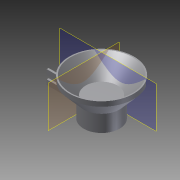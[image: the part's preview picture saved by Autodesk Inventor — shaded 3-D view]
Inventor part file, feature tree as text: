
AUTODESK INVENTOR PART (.ipt)
format: ipt  version: 2012 (Build 160160000, 160)  size: 119,808 bytes
history: native  units: in
note: dims shown in document units (in); Inventor stores cm internally (conversion verified against a paired STEP export)
features: plane x3, sketch x3, reference x3, extrude x2, revolve x1
ambient origin geometry x8: Origin, YZ Plane, XZ Plane, XY Plane, X Axis, Y Axis, Z Axis, Center Point
bodies: Solid1 (feature_tree)
feature tree (12):
  revolve  "Revolution1"  [1 undecoded]
  plane  "Work Plane1"
  extrude  "Extrusion1"  Depth=0.0394in
  plane  "Work Plane3"
  extrude  "Extrusion2"  Depth=0.0812in TaperAngle=0.0deg
  sketch  "Sketch1"  dims[d0=90.0deg d1=0.1969in]
  reference  "Reference1"
  sketch  "Sketch2"  dims[d2=0.0787in d3=0.0394in]
  reference  "Reference2"
  plane  "Work Plane2"
  sketch  "Sketch3"  dims[d4=0.1575in d6=0.0812in d7=1.5094in d8=0.0in d9=0.0in d10=0.0197in d11=0.4562in d12=0.2281in d13=0.0in d14=0.0in]
  reference  "Reference3"
note: 1 required parameter value undecoded (feature->parameter linkage not recoverable at this tier; creation-order binding heuristic only, values carry confidence <= 0.55)
